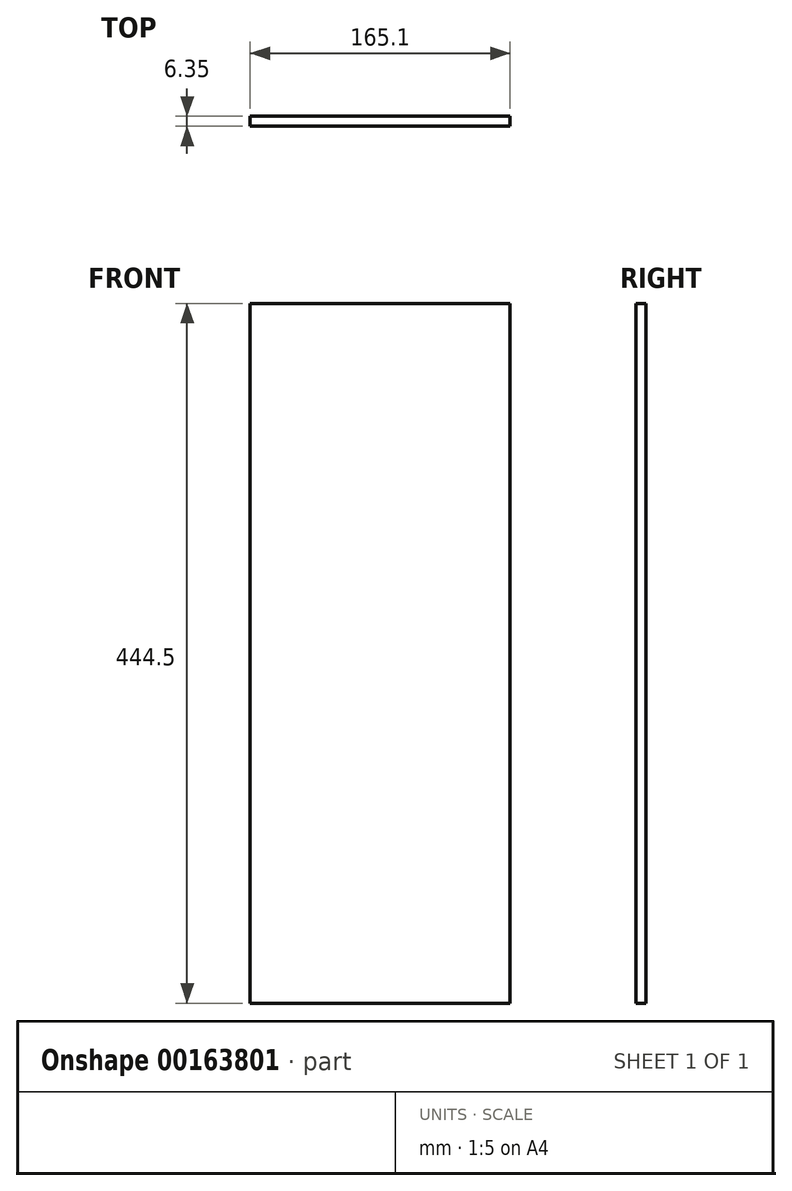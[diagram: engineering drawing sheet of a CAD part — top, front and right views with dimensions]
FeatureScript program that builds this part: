
annotation { "Feature Type Name" : "Feature", "Feature Type Description" : "" }
export const myFeature = defineFeature(function(context is Context, id is Id, definition is map)
    precondition{}
    {
        {
            var Q0;
            Q0=qCreatedBy(makeId("Front.planeOp"),FACE);
            var sketch = newSketch(context, id + "F0", { "sketchPlane" : qUnion([Q0])});
            skLineSegment(sketch, "E0.bottom", {"start": v(-82.55, -222.25) * mm, "end": v(82.55, -222.25) * mm});
            skLineSegment(sketch, "E0.top", {"start": v(-82.55, 222.25) * mm, "end": v(82.55, 222.25) * mm});
            skLineSegment(sketch, "E0.left", {"start": v(-82.55, -222.25) * mm, "end": v(-82.55, 222.25) * mm});
            skLineSegment(sketch, "E0.right", {"start": v(82.55, -222.25) * mm, "end": v(82.55, 222.25) * mm});
            skPoint(sketch, "E0.middle", {"position": v(0, 0) * mm});
            skSolve(sketch);
        }
        {
            var Q0;
            Q0=qSketchRegion(id+"F0",true);
            extrude(context, id + "F1", {"entities" : qUnion([Q0]), "depth" : 6.35 * mm});
        }
    });
